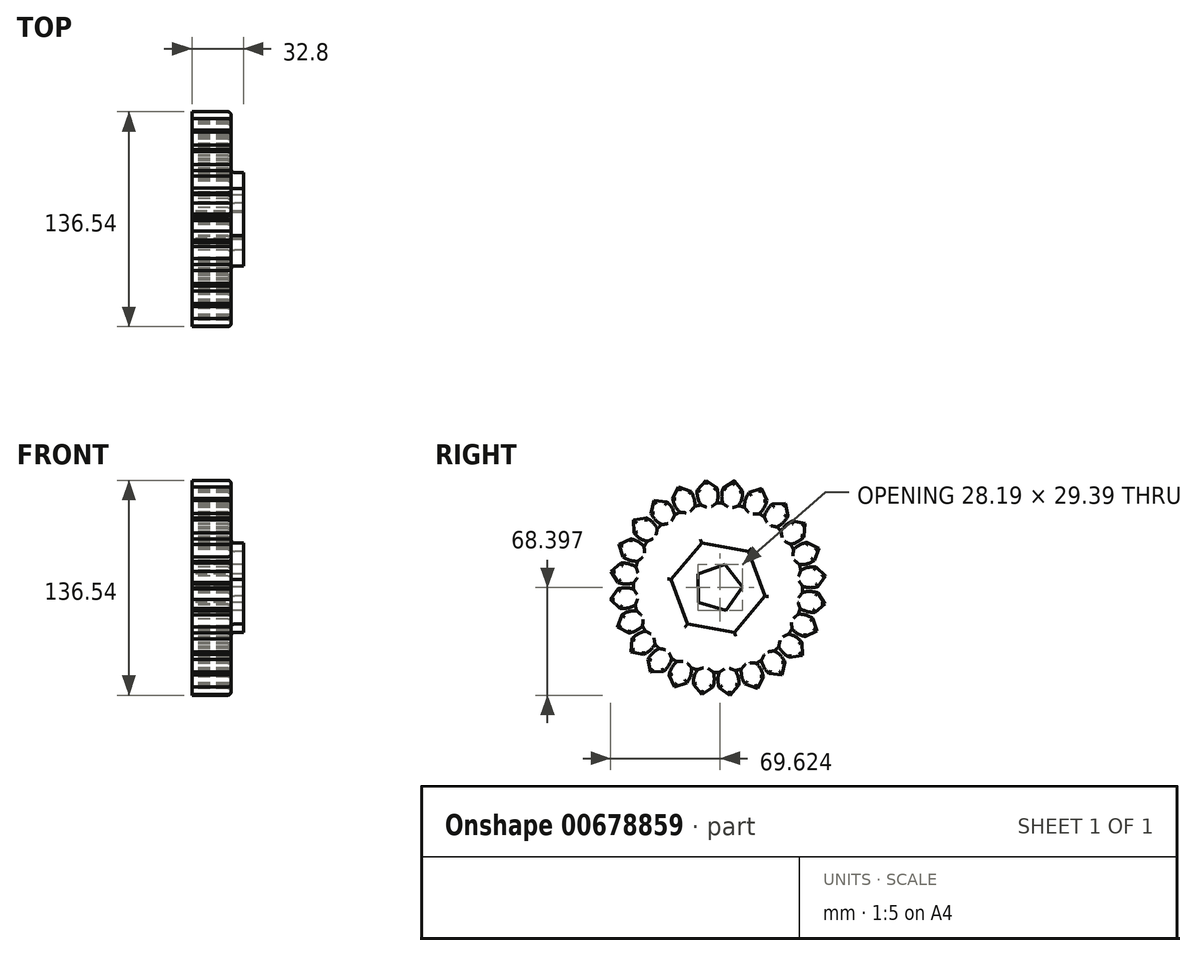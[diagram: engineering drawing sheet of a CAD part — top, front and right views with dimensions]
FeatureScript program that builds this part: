
annotation { "Feature Type Name" : "Feature", "Feature Type Description" : "" }
export const myFeature = defineFeature(function(context is Context, id is Id, definition is map)
    precondition{}
    {
        {
            var Q0;
            Q0=qCreatedBy(makeId("Right.planeOp"),FACE);
            var sketch = newSketch(context, id + "F0", { "sketchPlane" : qUnion([Q0])});
            skCircle(sketch, "E0", {"center": v(0, 0) * mm, "radius": 53.72 * mm});
            skCircle(sketch, "E1", {"center": v(0, 0) * mm, "radius": 58.67 * mm, "construction": true});
            skCircle(sketch, "E2", {"center": v(0, 0) * mm, "radius": 63.5 * mm, "construction": true});
            skLineSegment(sketch, "E3", {"start": v(0, 0) * mm, "end": v(0, 53.72) * mm, "construction": true});
            skLineSegment(sketch, "E4", {"start": v(0, 0) * mm, "end": v(-3.51, 53.6) * mm, "construction": true});
            skLineSegment(sketch, "E5", {"start": v(0, 0) * mm, "end": v(0, 101.28) * mm, "construction": true});
            skLineSegment(sketch, "E6", {"start": v(0, 58.67) * mm, "end": v(-92.4, 58.67) * mm});
            skLineSegment(sketch, "E7", {"start": v(0, 58.67) * mm, "end": v(-84.2, 28.03) * mm, "construction": true});
            skCircle(sketch, "E8", {"center": v(0, 58.67) * mm, "radius": 14.6 * mm, "construction": true});
            skCircle(sketch, "E9", {"center": v(-14.6, 58.67) * mm, "radius": 14.6 * mm, "construction": true});
            skArc(sketch, "E10", {"start": v(-0.87, 53.71) * mm, "mid": v(0, 58.6) * mm, "end": v(-0.82, 63.5) * mm});
            skLineSegment(sketch, "E11", {"start": v(-7.68, 68.33) * mm, "end": v(-0.82, 63.5) * mm});
            skLineSegment(sketch, "E12", {"start": v(0, 0) * mm, "end": v(-11.2, 100.77) * mm, "construction": true});
            skLineSegment(sketch, "E13.MirrorCS", {"start": v(-7.51, 68.35) * mm, "end": v(-13.15, 62.12) * mm});
            skArc(sketch, "E14.MirrorCS", {"start": v(-10.95, 52.6) * mm, "mid": v(-12.87, 57.17) * mm, "end": v(-13.15, 62.12) * mm});
            skCircle(sketch, "E15.cCircle", {"center": v(0, 0) * mm, "radius": 26.14 * mm, "construction": true});
            skLineSegment(sketch, "E15.0", {"start": v(19.4, 23.12) * mm, "end": v(29.72, -5.24) * mm});
            skLineSegment(sketch, "E15.1", {"start": v(29.72, -5.24) * mm, "end": v(10.32, -28.36) * mm});
            skLineSegment(sketch, "E15.2", {"start": v(10.32, -28.36) * mm, "end": v(-19.4, -23.12) * mm});
            skLineSegment(sketch, "E15.3", {"start": v(-19.4, -23.12) * mm, "end": v(-29.72, 5.24) * mm});
            skLineSegment(sketch, "E15.4", {"start": v(-29.72, 5.24) * mm, "end": v(-10.32, 28.36) * mm});
            skLineSegment(sketch, "E15.5", {"start": v(-10.32, 28.36) * mm, "end": v(19.4, 23.12) * mm});
            skPoint(sketch, "E15.0.midPoint", {"position": v(24.56, 8.94) * mm});
            skCircle(sketch, "E16.cCircle", {"center": v(0, 0) * mm, "radius": 12.5 * mm, "construction": true});
            skLineSegment(sketch, "E16.0", {"start": v(4.38, 14.82) * mm, "end": v(15.45, 0.41) * mm});
            skLineSegment(sketch, "E16.1", {"start": v(15.45, 0.41) * mm, "end": v(5.17, -14.57) * mm});
            skLineSegment(sketch, "E16.2", {"start": v(5.17, -14.57) * mm, "end": v(-12.26, -9.41) * mm});
            skLineSegment(sketch, "E16.3", {"start": v(-12.26, -9.41) * mm, "end": v(-12.74, 8.75) * mm});
            skLineSegment(sketch, "E16.4", {"start": v(-12.74, 8.75) * mm, "end": v(4.38, 14.82) * mm});
            skPoint(sketch, "E16.0.midPoint", {"position": v(9.92, 7.62) * mm});
            skSolve(sketch);
        }
        {
            var Q0;
            Q0 = qSketchRegion(id + "F0", true);
            extrude(context, id + "F1", {"entities" : qUnion([Q0]), "depth" : 25 * mm, "offsetDistance" : 25 * mm});
        }
        {
            var Q0;
            Q0=makeQuery(id+"F1.opExtrude","SWEPT_BODY",BODY,{"disambiguationData":[OSD([sQuery(id+"F0.wireOp",EDGE,"E0"),sQuery(id+"F0.wireOp",EDGE,"E10"),sQuery(id+"F0.wireOp",EDGE,"E11"),sQuery(id+"F0.wireOp",EDGE,"E13.MirrorCS"),sQuery(id+"F0.wireOp",EDGE,"E14.MirrorCS")])]});
            var Q1;
            Q1=makeQuery(id+"F1.opExtrude","SWEPT_FACE",FACE,{"disambiguationData":[OSD([sQuery(id+"F0.wireOp",EDGE,"E0")])]});
            circularPattern(context, id + "F2", {"entities" : qUnion([Q0]), "axis" : qUnion([Q1]), "angle" : 360 * degree, "instanceCount" : 24, "equalSpace" : true});
        }
        {
            var Q0;
            Q0=makeQuery(id+"F0.imprint","IMPRINT",FACE,{"disambiguationData":[TD([[makeQuery(id+"F0.imprint","IMPRINT",EDGE,{"derivedFrom":sQuery(id+"F0.wireOp",EDGE,"E15.0")}),-1.0]])]});
            extrude(context, id + "F3", {"entities" : qUnion([Q0]), "operationType" : NewBodyOperationType.ADD, "depth" : 32.8 * mm, "offsetDistance" : 25 * mm});
        }
        {
            var Q0;
            {var subQ0=makeQuery(id+"F1.opExtrude","CAP_FACE",FACE,{"disambiguationData":[OSD([sQuery(id+"F0.wireOp",EDGE,"E0"),sQuery(id+"F0.wireOp",EDGE,"E10"),sQuery(id+"F0.wireOp",EDGE,"E11"),sQuery(id+"F0.wireOp",EDGE,"E13.MirrorCS"),sQuery(id+"F0.wireOp",EDGE,"E14.MirrorCS"),sQuery(id+"F0.wireOp",EDGE,"E15.0"),sQuery(id+"F0.wireOp",EDGE,"E15.1"),sQuery(id+"F0.wireOp",EDGE,"E15.2"),sQuery(id+"F0.wireOp",EDGE,"E15.3"),sQuery(id+"F0.wireOp",EDGE,"E15.4"),sQuery(id+"F0.wireOp",EDGE,"E15.5")])],"isStart":false});Q0=makeQuery(id+"F3.boolean.opBoolean","MERGE",FACE,{"derivedFrom":[subQ0,makeQuery(id+"F2.opPattern","COPY",FACE,{"derivedFrom":subQ0,"instanceName":"1"}),makeQuery(id+"F2.opPattern","COPY",FACE,{"derivedFrom":subQ0,"instanceName":"2"}),makeQuery(id+"F2.opPattern","COPY",FACE,{"derivedFrom":subQ0,"instanceName":"3"}),makeQuery(id+"F2.opPattern","COPY",FACE,{"derivedFrom":subQ0,"instanceName":"4"}),makeQuery(id+"F2.opPattern","COPY",FACE,{"derivedFrom":subQ0,"instanceName":"5"}),makeQuery(id+"F2.opPattern","COPY",FACE,{"derivedFrom":subQ0,"instanceName":"6"}),makeQuery(id+"F2.opPattern","COPY",FACE,{"derivedFrom":subQ0,"instanceName":"7"}),makeQuery(id+"F2.opPattern","COPY",FACE,{"derivedFrom":subQ0,"instanceName":"8"}),makeQuery(id+"F2.opPattern","COPY",FACE,{"derivedFrom":subQ0,"instanceName":"9"}),makeQuery(id+"F2.opPattern","COPY",FACE,{"derivedFrom":subQ0,"instanceName":"10"}),makeQuery(id+"F2.opPattern","COPY",FACE,{"derivedFrom":subQ0,"instanceName":"11"}),makeQuery(id+"F2.opPattern","COPY",FACE,{"derivedFrom":subQ0,"instanceName":"12"}),makeQuery(id+"F2.opPattern","COPY",FACE,{"derivedFrom":subQ0,"instanceName":"13"}),makeQuery(id+"F2.opPattern","COPY",FACE,{"derivedFrom":subQ0,"instanceName":"14"}),makeQuery(id+"F2.opPattern","COPY",FACE,{"derivedFrom":subQ0,"instanceName":"15"}),makeQuery(id+"F2.opPattern","COPY",FACE,{"derivedFrom":subQ0,"instanceName":"16"}),makeQuery(id+"F2.opPattern","COPY",FACE,{"derivedFrom":subQ0,"instanceName":"17"}),makeQuery(id+"F2.opPattern","COPY",FACE,{"derivedFrom":subQ0,"instanceName":"18"}),makeQuery(id+"F2.opPattern","COPY",FACE,{"derivedFrom":subQ0,"instanceName":"19"}),makeQuery(id+"F2.opPattern","COPY",FACE,{"derivedFrom":subQ0,"instanceName":"20"}),makeQuery(id+"F2.opPattern","COPY",FACE,{"derivedFrom":subQ0,"instanceName":"21"}),makeQuery(id+"F2.opPattern","COPY",FACE,{"derivedFrom":subQ0,"instanceName":"22"}),makeQuery(id+"F2.opPattern","COPY",FACE,{"derivedFrom":subQ0,"instanceName":"23"})]});}
            var Q1;
            Q1=makeQuery(id+"F2.opPattern","COPY",EDGE,{"derivedFrom":makeQuery(id+"F1.opExtrude","CAP_EDGE",EDGE,{"disambiguationData":[OSD([sQuery(id+"F0.wireOp",EDGE,"E10")])],"isStart":false}),"instanceName":"22"});
            fillet(context, id + "F4", {"entities" : qUnion([Q0, Q1]), "radius" : 2 * mm, "tangentPropagation" : true, "allowEdgeOverflow" : false});
        }
    });
